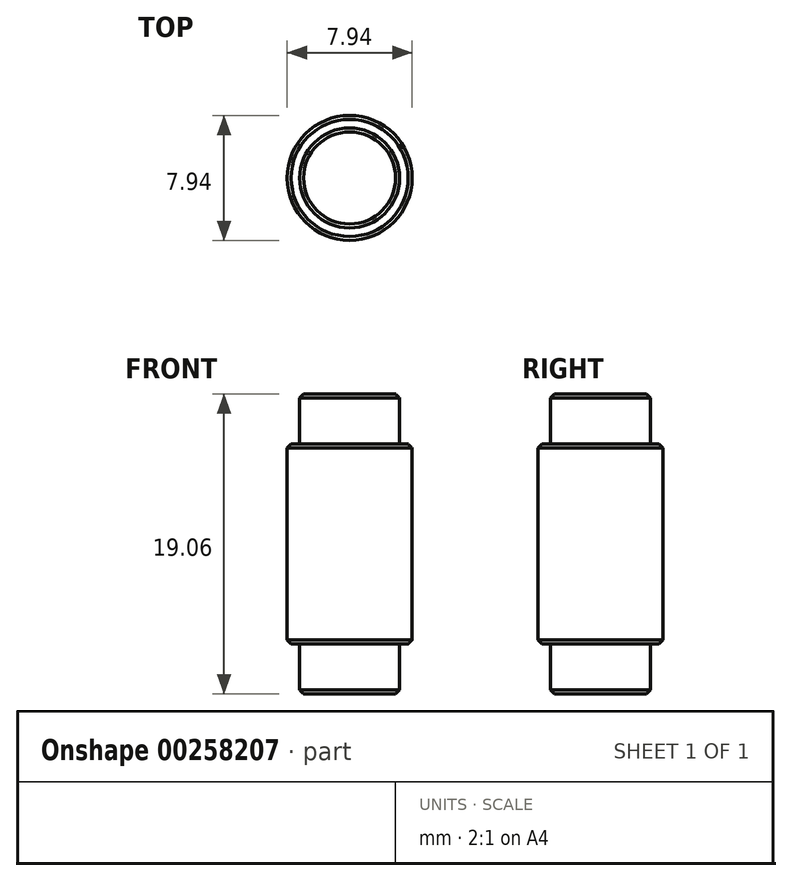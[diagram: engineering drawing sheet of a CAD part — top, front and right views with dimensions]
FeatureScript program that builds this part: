
annotation { "Feature Type Name" : "Feature", "Feature Type Description" : "" }
export const myFeature = defineFeature(function(context is Context, id is Id, definition is map)
    precondition{}
    {
        {
            var Q0;
            Q0=qCreatedBy(makeId("Top.planeOp"),FACE);
            var sketch = newSketch(context, id + "F0", { "sketchPlane" : qUnion([Q0])});
            skCircle(sketch, "E0", {"center": v(0, 0) * mm, "radius": 3.97 * mm});
            skSolve(sketch);
        }
        {
            var Q0;
            Q0 = qSketchRegion(id + "F0", true);
            extrude(context, id + "F1", {"entities" : qUnion([Q0]), "depth" : 6.35 * mm});
        }
        {
            var Q0;
            Q0=makeQuery(id+"F1.opExtrude","CAP_FACE",FACE,{"disambiguationData":[OSD([sQuery(id+"F0.wireOp",EDGE,"E0")])],"isStart":false});
            var sketch = newSketch(context, id + "F2", { "sketchPlane" : qUnion([Q0])});
            skCircle(sketch, "E1", {"center": v(0, 0) * mm, "radius": 3.18 * mm});
            skSolve(sketch);
        }
        {
            var Q0;
            Q0 = qSketchRegion(id + "F2", true);
            extrude(context, id + "F3", {"entities" : qUnion([Q0]), "operationType" : NewBodyOperationType.ADD, "depth" : 3.17 * mm});
        }
        {
            var Q0;
            Q0=makeQuery(id+"F1.opExtrude","CAP_FACE",FACE,{"disambiguationData":[OSD([sQuery(id+"F0.wireOp",EDGE,"E0")])],"isStart":true});
            extrude(context, id + "F4", {"entities" : qUnion([Q0]), "operationType" : NewBodyOperationType.ADD, "depth" : 6.35 * mm});
        }
        {
            var Q0;
            Q0=makeQuery(id+"F4.opExtrude","CAP_FACE",FACE,{"disambiguationData":[OSD([sQuery(id+"F0.wireOp",EDGE,"E0")])],"isStart":false});
            var sketch = newSketch(context, id + "F5", { "sketchPlane" : qUnion([Q0])});
            skCircle(sketch, "E2", {"center": v(0, 0) * mm, "radius": 3.18 * mm});
            skSolve(sketch);
        }
        {
            var Q0;
            Q0 = qSketchRegion(id + "F5", true);
            extrude(context, id + "F6", {"entities" : qUnion([Q0]), "operationType" : NewBodyOperationType.ADD, "depth" : 3.17 * mm});
        }
        {
            var Q0;
            Q0=makeQuery(id+"F3.opExtrude","CAP_EDGE",EDGE,{"disambiguationData":[OSD([sQuery(id+"F2.wireOp",EDGE,"E1")])],"isStart":false});
            var Q1;
            Q1=makeQuery(id+"F1.opExtrude","CAP_EDGE",EDGE,{"disambiguationData":[OSD([sQuery(id+"F0.wireOp",EDGE,"E0")])],"isStart":false});
            var Q2;
            Q2=makeQuery(id+"F4.opExtrude","CAP_EDGE",EDGE,{"disambiguationData":[OSD([sQuery(id+"F0.wireOp",EDGE,"E0")])],"isStart":false});
            var Q3;
            Q3=makeQuery(id+"F6.opExtrude","CAP_EDGE",EDGE,{"disambiguationData":[OSD([sQuery(id+"F5.wireOp",EDGE,"E2")])],"isStart":false});
            chamfer(context, id + "F7", {"entities" : qUnion([Q0, Q1, Q2, Q3]), "width" : 0.25 * mm, "tangentPropagation" : true});
        }
    });
